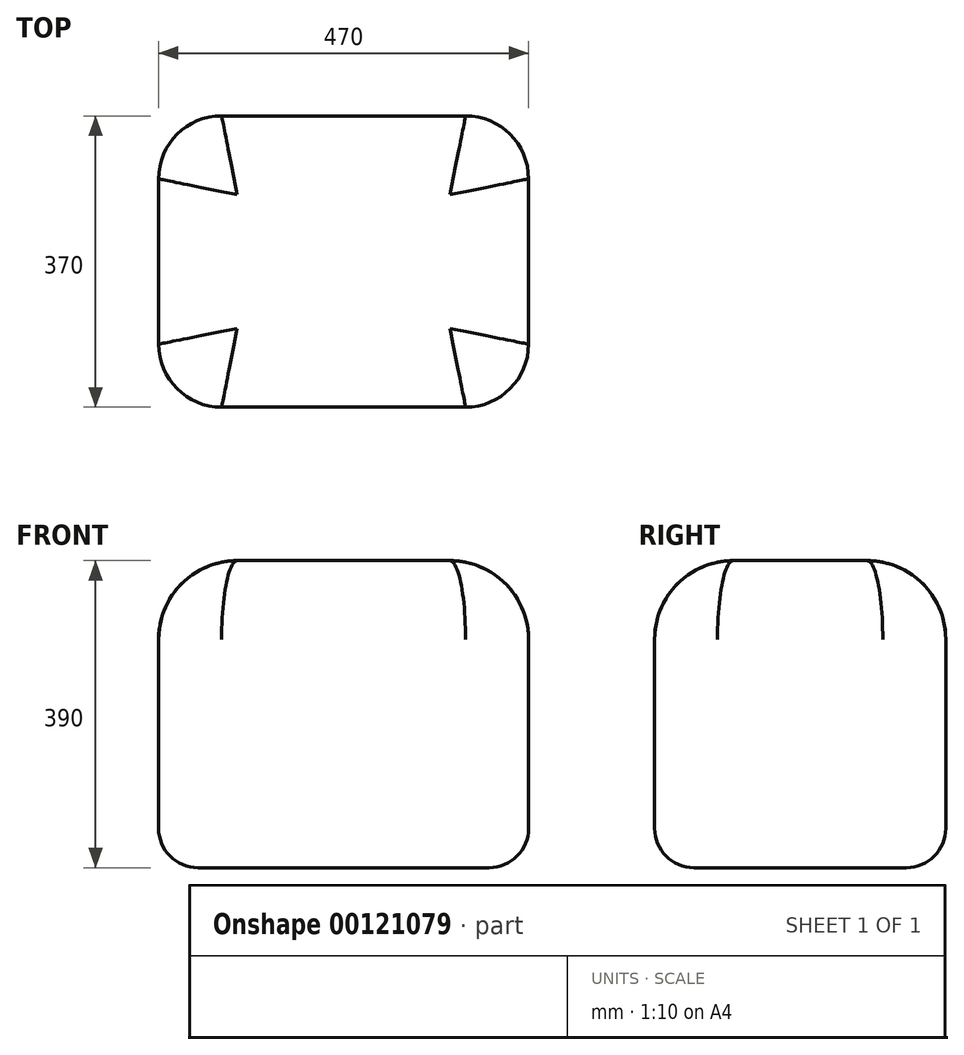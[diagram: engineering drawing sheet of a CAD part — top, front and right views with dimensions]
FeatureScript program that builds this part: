
annotation { "Feature Type Name" : "Feature", "Feature Type Description" : "" }
export const myFeature = defineFeature(function(context is Context, id is Id, definition is map)
    precondition{}
    {
        {
            var Q0;
            Q0=qCreatedBy(makeId("Top.planeOp"),FACE);
            var sketch = newSketch(context, id + "F0", { "sketchPlane" : qUnion([Q0])});
            skLineSegment(sketch, "E0.bottom", {"start": v(155, 185) * mm, "end": v(-155, 185) * mm});
            skLineSegment(sketch, "E0.top", {"start": v(155, -185) * mm, "end": v(-155, -185) * mm});
            skLineSegment(sketch, "E0.left", {"start": v(235, 105) * mm, "end": v(235, -105) * mm});
            skLineSegment(sketch, "E0.right", {"start": v(-235, 105) * mm, "end": v(-235, -105) * mm});
            skPoint(sketch, "E0.middle", {"position": v(0, 0) * mm});
            skPoint(sketch, "E1.visualSharp", {"position": v(-235, 185) * mm});
            skArc(sketch, "E1.filletArc", {"start": v(-155, 185) * mm, "mid": v(-211.57, 161.57) * mm, "end": v(-235, 105) * mm});
            skPoint(sketch, "E2.visualSharp", {"position": v(-235, -185) * mm});
            skArc(sketch, "E2.filletArc", {"start": v(-235, -105) * mm, "mid": v(-211.57, -161.57) * mm, "end": v(-155, -185) * mm});
            skPoint(sketch, "E3.visualSharp", {"position": v(235, -185) * mm});
            skArc(sketch, "E3.filletArc", {"start": v(155, -185) * mm, "mid": v(211.57, -161.57) * mm, "end": v(235, -105) * mm});
            skPoint(sketch, "E4.visualSharp", {"position": v(235, 185) * mm});
            skArc(sketch, "E4.filletArc", {"start": v(235, 105) * mm, "mid": v(211.57, 161.57) * mm, "end": v(155, 185) * mm});
            skSolve(sketch);
        }
        {
            var Q0;
            Q0=makeQuery(id+"F0.imprint","IMPRINT",FACE,{"disambiguationData":[TD([[makeQuery(id+"F0.imprint","IMPRINT",EDGE,{"derivedFrom":sQuery(id+"F0.wireOp",EDGE,"E0.bottom")}),1.0]])]});
            extrude(context, id + "F1", {"entities" : qUnion([Q0]), "depth" : 390 * mm});
        }
        {
            var Q0;
            Q0=makeQuery(id+"F1.opExtrude","CAP_FACE",FACE,{"disambiguationData":[OSD([sQuery(id+"F0.wireOp",EDGE,"E0.bottom"),sQuery(id+"F0.wireOp",EDGE,"E0.top"),sQuery(id+"F0.wireOp",EDGE,"E0.left"),sQuery(id+"F0.wireOp",EDGE,"E0.right"),sQuery(id+"F0.wireOp",EDGE,"E1.filletArc"),sQuery(id+"F0.wireOp",EDGE,"E2.filletArc"),sQuery(id+"F0.wireOp",EDGE,"E3.filletArc"),sQuery(id+"F0.wireOp",EDGE,"E4.filletArc")])],"isStart":false});
            fillet(context, id + "F2", {"entities" : qUnion([Q0]), "radius" : 100 * mm, "tangentPropagation" : true, "allowEdgeOverflow" : false});
        }
        {
            var Q0;
            Q0=makeQuery(id+"F1.opExtrude","CAP_FACE",FACE,{"disambiguationData":[OSD([sQuery(id+"F0.wireOp",EDGE,"E0.bottom"),sQuery(id+"F0.wireOp",EDGE,"E0.top"),sQuery(id+"F0.wireOp",EDGE,"E0.left"),sQuery(id+"F0.wireOp",EDGE,"E0.right"),sQuery(id+"F0.wireOp",EDGE,"E1.filletArc"),sQuery(id+"F0.wireOp",EDGE,"E2.filletArc"),sQuery(id+"F0.wireOp",EDGE,"E3.filletArc"),sQuery(id+"F0.wireOp",EDGE,"E4.filletArc")])],"isStart":true});
            fillet(context, id + "F3", {"entities" : qUnion([Q0]), "radius" : 50 * mm, "tangentPropagation" : true, "allowEdgeOverflow" : false});
        }
    });
